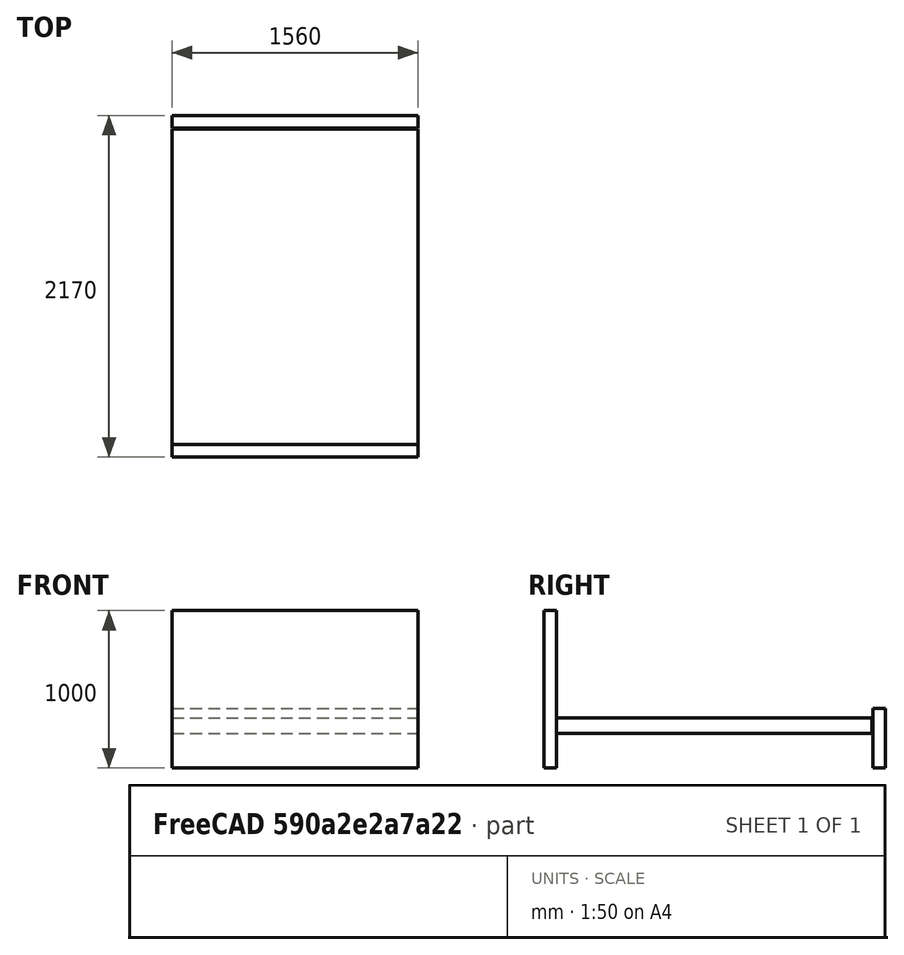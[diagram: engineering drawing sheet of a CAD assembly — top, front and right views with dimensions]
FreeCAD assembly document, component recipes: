
FREECAD ASSEMBLY — COMPONENT RECIPES ("mueble_con_ensamblaje_y_planos")

This assembly document has 3 components, labeled P0..P2 below (a component is one placed body or linked part). 0 of them carry a construction recipe — the FreeCAD feature program that regenerates the part from scratch, quoted from this document or its linked companion documents; the rest are supplied as boundary geometry only. No exploded tour is included for this assembly.
COMPONENT P0 — geometry summary ("cabecero"; no construction recipe available for this part):
  bounding box: 1560.0 x 1000.0 x 80.0 mm
  tessellated surface: 12 triangles
  volume: 124800000 mm^3 (100% of its bounding box)
  symmetry: 2-fold rotationally symmetric about the x axis; 2-fold rotationally symmetric about the z axis; mirror-symmetric across its x mid-plane, y mid-plane, z mid-plane
COMPONENT P1 — geometry summary ("pies_de_la_cama"; no construction recipe available for this part):
  bounding box: 1560.0 x 380.0 x 80.0 mm
  tessellated surface: 12 triangles
  volume: 47424000 mm^3 (100% of its bounding box)
  symmetry: 2-fold rotationally symmetric about the y axis; 2-fold rotationally symmetric about the z axis; mirror-symmetric across its x mid-plane, y mid-plane, z mid-plane
COMPONENT P2 — geometry summary ("armadura"; no construction recipe available for this part):
  bounding box: 2004.0 x 1560.0 x 100.0 mm
  tessellated surface: 12 triangles
  volume: 312624000 mm^3 (100% of its bounding box)
  symmetry: 2-fold rotationally symmetric about the x axis; 2-fold rotationally symmetric about the y axis; 2-fold rotationally symmetric about the z axis; mirror-symmetric across its y mid-plane, z mid-plane
PROVENANCE & LICENSES
A FreeCAD (.FCStd) document from a public repository crawl; recipes are the document's own serialized feature recipes (and, for linked parts, companion documents' recipes).
License: gpl-3.0.
